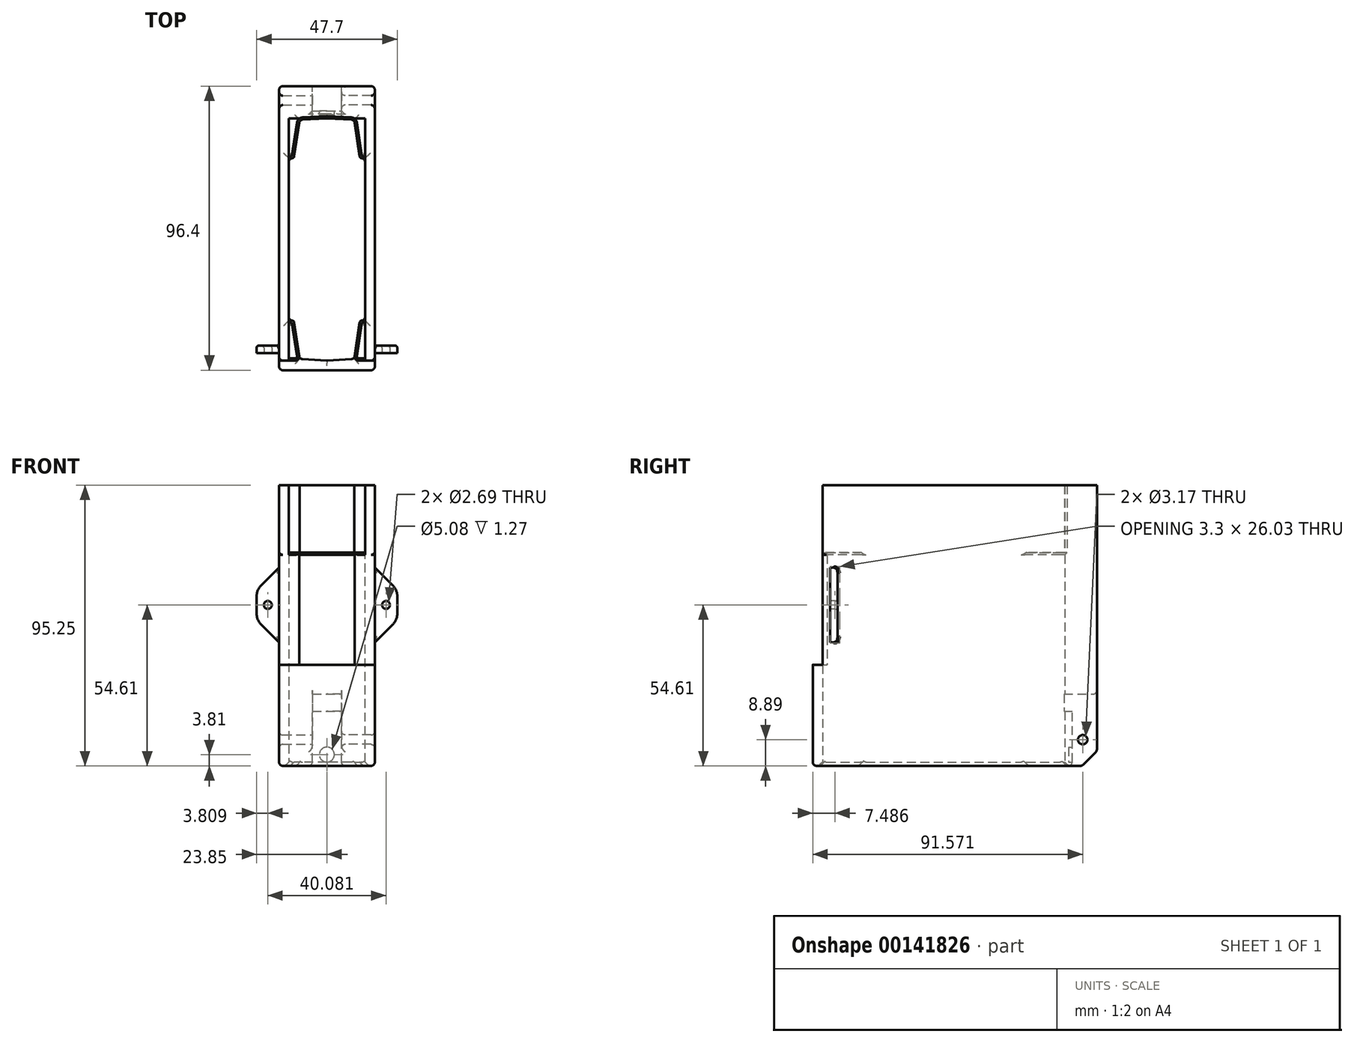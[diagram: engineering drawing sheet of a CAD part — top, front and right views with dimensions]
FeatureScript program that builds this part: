
annotation { "Feature Type Name" : "Feature", "Feature Type Description" : "" }
export const myFeature = defineFeature(function(context is Context, id is Id, definition is map)
    precondition{}
    {
        {
            var Q0;
            Q0=qCreatedBy(makeId("Top.planeOp"),FACE);
            var sketch = newSketch(context, id + "F0", { "sketchPlane" : qUnion([Q0])});
            skLineSegment(sketch, "E0.left", {"start": v(12.94, -27.53) * mm, "end": v(12.94, 27.53) * mm});
            skLineSegment(sketch, "E0.right", {"start": v(-12.94, -27.53) * mm, "end": v(-12.94, 27.53) * mm});
            skPoint(sketch, "E0.middle", {"position": v(0, 0) * mm});
            skLineSegment(sketch, "E1.top", {"start": v(12.94, -27.53) * mm, "end": v(11.21, -27.53) * mm});
            skPoint(sketch, "E2.orphan", {"position": v(12.94, -41.05) * mm});
            skLineSegment(sketch, "E3", {"start": v(11.21, -27.53) * mm, "end": v(9.28, -40.56) * mm});
            skLineSegment(sketch, "E4", {"start": v(0, -41.1) * mm, "end": v(9.28, -40.56) * mm});
            skPoint(sketch, "E0.bottom.start.orphan", {"position": v(11.21, -41.05) * mm});
            skPoint(sketch, "E5.orphan", {"position": v(9.2, -41.05) * mm});
            skLineSegment(sketch, "E6.MirrorCS", {"start": v(0, -41.1) * mm, "end": v(-9.28, -40.56) * mm});
            skLineSegment(sketch, "E7.MirrorCS", {"start": v(-11.21, -27.53) * mm, "end": v(-9.28, -40.56) * mm});
            skLineSegment(sketch, "E8.MirrorCS", {"start": v(-12.94, -27.53) * mm, "end": v(-11.21, -27.53) * mm});
            skLineSegment(sketch, "E9.MirrorCS", {"start": v(-12.94, 27.53) * mm, "end": v(-11.21, 27.53) * mm});
            skLineSegment(sketch, "E10.MirrorCS", {"start": v(-11.21, 27.53) * mm, "end": v(-9.28, 40.56) * mm});
            skLineSegment(sketch, "E11.MirrorCS", {"start": v(0, 41.1) * mm, "end": v(-9.28, 40.56) * mm});
            skLineSegment(sketch, "E12.MirrorCS", {"start": v(0, 41.1) * mm, "end": v(9.28, 40.56) * mm});
            skLineSegment(sketch, "E13.MirrorCS", {"start": v(11.21, 27.53) * mm, "end": v(9.28, 40.56) * mm});
            skLineSegment(sketch, "E14.MirrorCS", {"start": v(12.94, 27.53) * mm, "end": v(11.21, 27.53) * mm});
            skPoint(sketch, "E15.orphan", {"position": v(-12.94, -41.1) * mm});
            skPoint(sketch, "E16.orphan", {"position": v(-12.94, 41.05) * mm});
            skPoint(sketch, "E17.orphan", {"position": v(12.94, 41.1) * mm});
            skLineSegment(sketch, "E18.bottom", {"start": v(16.23, -44.39) * mm, "end": v(-16.23, -44.39) * mm});
            skLineSegment(sketch, "E18.top", {"start": v(16.23, 44.39) * mm, "end": v(-16.23, 44.39) * mm});
            skLineSegment(sketch, "E18.left", {"start": v(16.23, -44.39) * mm, "end": v(16.23, 44.39) * mm});
            skLineSegment(sketch, "E18.right", {"start": v(-16.23, -44.39) * mm, "end": v(-16.23, 44.39) * mm});
            skLineSegment(sketch, "E19", {"start": v(0, -41.1) * mm, "end": v(0, 41.1) * mm});
            skSolve(sketch);
        }
        {
            var Q0;
            Q0=makeQuery(id+"F0.imprint","IMPRINT",FACE,{"disambiguationData":[TD([[makeQuery(id+"F0.imprint","IMPRINT",EDGE,{"derivedFrom":sQuery(id+"F0.wireOp",EDGE,"E0.left")}),-1.0]])]});
            extrude(context, id + "F1", {"entities" : qUnion([Q0]), "depth" : 72.39 * mm});
        }
        {
            var Q0;
            Q0=makeQuery(id+"F1.opExtrude","SWEPT_FACE",FACE,{"disambiguationData":[OSD([sQuery(id+"F0.wireOp",EDGE,"E18.top")])]});
            var sketch = newSketch(context, id + "F2", { "sketchPlane" : qUnion([Q0])});
            skLineSegment(sketch, "E20.bottom", {"start": v(4.95, 24.36) * mm, "end": v(-4.95, 24.36) * mm});
            skLineSegment(sketch, "E20.top", {"start": v(4.95, 18.52) * mm, "end": v(-4.95, 18.52) * mm});
            skLineSegment(sketch, "E20.left", {"start": v(4.95, 24.36) * mm, "end": v(4.95, 18.52) * mm});
            skLineSegment(sketch, "E20.right", {"start": v(-4.95, 24.36) * mm, "end": v(-4.95, 18.52) * mm});
            skPoint(sketch, "E20.middle", {"position": v(0, 21.44) * mm});
            skSolve(sketch);
        }
        {
            var Q0;
            Q0=makeQuery(id+"F2.imprint","IMPRINT",FACE,{"disambiguationData":[TD([[makeQuery(id+"F2.imprint","IMPRINT",EDGE,{"derivedFrom":sQuery(id+"F2.wireOp",EDGE,"E20.bottom")}),1.0]])]});
            extrude(context, id + "F3", {"entities" : qUnion([Q0]), "operationType" : NewBodyOperationType.REMOVE, "endBound" : BoundingType.UP_TO_NEXT, "oppositeDirection" : true, "depth" : 25.4 * mm});
        }
        {
            var Q0;
            Q0=makeQuery(id+"F1.opExtrude","SWEPT_FACE",FACE,{"disambiguationData":[OSD([sQuery(id+"F0.wireOp",EDGE,"E18.top")])]});
            extrude(context, id + "F4", {"entities" : qUnion([Q0]), "operationType" : NewBodyOperationType.ADD, "depth" : 7.62 * mm});
        }
        {
            var Q0;
            {var subQ0=sQuery(id+"F0.wireOp",EDGE,"E18.top");Q0=makeQuery(id+"F4.opExtrude","CAP_EDGE",EDGE,{"disambiguationData":[OSD([subQ0]),TDD([makeQuery(id+"F1.opExtrude","CAP_EDGE",EDGE,{"disambiguationData":[OSD([subQ0])],"isStart":true})])],"isStart":false});}
            chamfer(context, id + "F5", {"entities" : qUnion([Q0]), "width" : 5.08 * mm, "tangentPropagation" : true});
        }
        {
            var Q0;
            {var subQ0=sQuery(id+"F2.wireOp",EDGE,"E20.top");Q0=makeQuery(id+"F4.boolean.opBoolean","MERGE",FACE,{"derivedFrom":[makeQuery(id+"F3.boolean.opBoolean","COPY",FACE,{"derivedFrom":makeQuery(id+"F3.opExtrude","SWEPT_FACE",FACE,{"disambiguationData":[OSD([subQ0])]})}),makeQuery(id+"F4.opExtrude","SWEPT_FACE",FACE,{"disambiguationData":[OSD([subQ0])]})]});}
            var sketch = newSketch(context, id + "F6", { "sketchPlane" : qUnion([Q0])});
            skLineSegment(sketch, "E21.bottom", {"start": v(-4.95, 52) * mm, "end": v(4.95, 52) * mm});
            skLineSegment(sketch, "E21.top", {"start": v(-4.95, 43.62) * mm, "end": v(4.95, 43.62) * mm});
            skLineSegment(sketch, "E21.left", {"start": v(-4.95, 52) * mm, "end": v(-4.95, 43.62) * mm});
            skLineSegment(sketch, "E21.right", {"start": v(4.95, 52) * mm, "end": v(4.95, 43.62) * mm});
            skSolve(sketch);
        }
        {
            var Q0;
            Q0=makeQuery(id+"F6.imprint","IMPRINT",FACE,{"disambiguationData":[TD([[makeQuery(id+"F6.imprint","IMPRINT",EDGE,{"derivedFrom":sQuery(id+"F6.wireOp",EDGE,"E21.bottom")}),-1.0]])]});
            extrude(context, id + "F7", {"entities" : qUnion([Q0]), "operationType" : NewBodyOperationType.REMOVE, "oppositeDirection" : true, "depth" : 25.4 * mm});
        }
        {
            var Q0;
            Q0=makeQuery(id+"F7.boolean.opBoolean","COPY",FACE,{"derivedFrom":makeQuery(id+"F7.opExtrude","SWEPT_FACE",FACE,{"disambiguationData":[OSD([sQuery(id+"F6.wireOp",EDGE,"E21.top")])]})});
            var sketch = newSketch(context, id + "F8", { "sketchPlane" : qUnion([Q0])});
            skCircle(sketch, "E22", {"center": v(0, 3.81) * mm, "radius": 2.54 * mm});
            skSolve(sketch);
        }
        {
            var Q0;
            Q0=makeQuery(id+"F8.imprint","IMPRINT",FACE,{"disambiguationData":[TD([[makeQuery(id+"F8.imprint","IMPRINT",EDGE,{"derivedFrom":sQuery(id+"F8.wireOp",EDGE,"E22")}),1.0]])]});
            extrude(context, id + "F9", {"entities" : qUnion([Q0]), "operationType" : NewBodyOperationType.REMOVE, "oppositeDirection" : true, "depth" : 1.27 * mm});
        }
        {
            var Q0;
            Q0=makeQuery(id+"F1.opExtrude","CAP_EDGE",EDGE,{"disambiguationData":[OSD([sQuery(id+"F0.wireOp",EDGE,"E0.right")])],"isStart":true});
            var Q1;
            Q1=makeQuery(id+"F1.opExtrude","CAP_EDGE",EDGE,{"disambiguationData":[OSD([sQuery(id+"F0.wireOp",EDGE,"E8.MirrorCS")])],"isStart":true});
            var Q2;
            Q2=makeQuery(id+"F1.opExtrude","CAP_EDGE",EDGE,{"disambiguationData":[OSD([sQuery(id+"F0.wireOp",EDGE,"E7.MirrorCS")])],"isStart":true});
            var Q3;
            Q3=makeQuery(id+"F1.opExtrude","CAP_EDGE",EDGE,{"disambiguationData":[OSD([sQuery(id+"F0.wireOp",EDGE,"E6.MirrorCS")])],"isStart":true});
            var Q4;
            Q4=makeQuery(id+"F1.opExtrude","CAP_EDGE",EDGE,{"disambiguationData":[OSD([sQuery(id+"F0.wireOp",EDGE,"E4")])],"isStart":true});
            var Q5;
            Q5=makeQuery(id+"F1.opExtrude","CAP_EDGE",EDGE,{"disambiguationData":[OSD([sQuery(id+"F0.wireOp",EDGE,"E3")])],"isStart":true});
            var Q6;
            Q6=makeQuery(id+"F1.opExtrude","CAP_EDGE",EDGE,{"disambiguationData":[OSD([sQuery(id+"F0.wireOp",EDGE,"E1.top")])],"isStart":true});
            var Q7;
            Q7=makeQuery(id+"F1.opExtrude","CAP_EDGE",EDGE,{"disambiguationData":[OSD([sQuery(id+"F0.wireOp",EDGE,"E0.left")])],"isStart":true});
            var Q8;
            Q8=makeQuery(id+"F1.opExtrude","CAP_EDGE",EDGE,{"disambiguationData":[OSD([sQuery(id+"F0.wireOp",EDGE,"E14.MirrorCS")])],"isStart":true});
            var Q9;
            Q9=makeQuery(id+"F1.opExtrude","CAP_EDGE",EDGE,{"disambiguationData":[OSD([sQuery(id+"F0.wireOp",EDGE,"E13.MirrorCS")])],"isStart":true});
            var Q10;
            Q10=makeQuery(id+"F1.opExtrude","CAP_EDGE",EDGE,{"disambiguationData":[OSD([sQuery(id+"F0.wireOp",EDGE,"E12.MirrorCS")])],"isStart":true});
            var Q11;
            Q11=makeQuery(id+"F1.opExtrude","CAP_EDGE",EDGE,{"disambiguationData":[OSD([sQuery(id+"F0.wireOp",EDGE,"E11.MirrorCS")])],"isStart":true});
            var Q12;
            Q12=makeQuery(id+"F1.opExtrude","CAP_EDGE",EDGE,{"disambiguationData":[OSD([sQuery(id+"F0.wireOp",EDGE,"E10.MirrorCS")])],"isStart":true});
            var Q13;
            Q13=makeQuery(id+"F1.opExtrude","CAP_EDGE",EDGE,{"disambiguationData":[OSD([sQuery(id+"F0.wireOp",EDGE,"E9.MirrorCS")])],"isStart":true});
            chamfer(context, id + "F10", {"entities" : qUnion([Q0, Q1, Q2, Q3, Q4, Q5, Q6, Q7, Q8, Q9, Q10, Q11, Q12, Q13]), "width" : 1.27 * mm, "tangentPropagation" : true});
        }
        {
            var Q0;
            Q0=makeQuery(id+"F1.opExtrude","SWEPT_EDGE",EDGE,{"disambiguationData":[OSD([sQuery(id+"F0.wireOp",EDGE,"E7.MirrorCS"),sQuery(id+"F0.wireOp",EDGE,"E8.MirrorCS")])]});
            var Q1;
            Q1=makeQuery(id+"F1.opExtrude","SWEPT_EDGE",EDGE,{"disambiguationData":[OSD([sQuery(id+"F0.wireOp",EDGE,"E1.top"),sQuery(id+"F0.wireOp",EDGE,"E3")])]});
            var Q2;
            Q2=makeQuery(id+"F1.opExtrude","SWEPT_EDGE",EDGE,{"disambiguationData":[OSD([sQuery(id+"F0.wireOp",EDGE,"E9.MirrorCS"),sQuery(id+"F0.wireOp",EDGE,"E10.MirrorCS")])]});
            var Q3;
            Q3=makeQuery(id+"F1.opExtrude","SWEPT_EDGE",EDGE,{"disambiguationData":[OSD([sQuery(id+"F0.wireOp",EDGE,"E13.MirrorCS"),sQuery(id+"F0.wireOp",EDGE,"E14.MirrorCS")])]});
            fillet(context, id + "F11", {"entities" : qUnion([Q0, Q1, Q2, Q3]), "radius" : 0.76 * mm, "tangentPropagation" : true, "allowEdgeOverflow" : false});
        }
        {
            var Q0;
            {var subQ0=sQuery(id+"F0.wireOp",EDGE,"E18.top");Q0=makeQuery(id+"F4.boolean.opBoolean","MERGE",FACE,{"derivedFrom":[makeQuery(id+"F1.opExtrude","CAP_FACE",FACE,{"disambiguationData":[OSD([sQuery(id+"F0.wireOp",EDGE,"E0.left"),sQuery(id+"F0.wireOp",EDGE,"E0.right"),sQuery(id+"F0.wireOp",EDGE,"E1.top"),sQuery(id+"F0.wireOp",EDGE,"E3"),sQuery(id+"F0.wireOp",EDGE,"E4"),sQuery(id+"F0.wireOp",EDGE,"E6.MirrorCS"),sQuery(id+"F0.wireOp",EDGE,"E7.MirrorCS"),sQuery(id+"F0.wireOp",EDGE,"E8.MirrorCS"),sQuery(id+"F0.wireOp",EDGE,"E9.MirrorCS"),sQuery(id+"F0.wireOp",EDGE,"E10.MirrorCS"),sQuery(id+"F0.wireOp",EDGE,"E11.MirrorCS"),sQuery(id+"F0.wireOp",EDGE,"E12.MirrorCS"),sQuery(id+"F0.wireOp",EDGE,"E13.MirrorCS"),sQuery(id+"F0.wireOp",EDGE,"E14.MirrorCS"),sQuery(id+"F0.wireOp",EDGE,"E18.bottom"),subQ0,sQuery(id+"F0.wireOp",EDGE,"E18.left"),sQuery(id+"F0.wireOp",EDGE,"E18.right")])],"isStart":true}),makeQuery(id+"F4.opExtrude","SWEPT_FACE",FACE,{"disambiguationData":[OSD([subQ0]),TDD([makeQuery(id+"F1.opExtrude","CAP_EDGE",EDGE,{"disambiguationData":[OSD([subQ0])],"isStart":true})])]})]});}
            var Q1;
            {var subQ0=sQuery(id+"F0.wireOp",EDGE,"E18.left");var subQ1=sQuery(id+"F0.wireOp",EDGE,"E18.top");Q1=makeQuery(id+"F5.opChamfer","BLEND_EDGE",EDGE,{"blendedFrom":[makeQuery(id+"F4.opExtrude","CAP_EDGE",EDGE,{"disambiguationData":[OSD([subQ1]),TDD([makeQuery(id+"F1.opExtrude","CAP_EDGE",EDGE,{"disambiguationData":[OSD([subQ1])],"isStart":true})])],"isStart":false}),makeQuery(id+"F4.boolean.opBoolean","MERGE",FACE,{"derivedFrom":[makeQuery(id+"F1.opExtrude","SWEPT_FACE",FACE,{"disambiguationData":[OSD([subQ0])]}),makeQuery(id+"F4.opExtrude","SWEPT_FACE",FACE,{"disambiguationData":[OSD([subQ1,subQ0])]})]})],"blendedInto":[makeQuery(id+"F4.boolean.opBoolean","MERGE",FACE,{"derivedFrom":[makeQuery(id+"F1.opExtrude","SWEPT_FACE",FACE,{"disambiguationData":[OSD([subQ0])]}),makeQuery(id+"F4.opExtrude","SWEPT_FACE",FACE,{"disambiguationData":[OSD([subQ1,subQ0])]})]})]});}
            var Q2;
            Q2=makeQuery(id+"F4.opExtrude","CAP_EDGE",EDGE,{"disambiguationData":[OSD([sQuery(id+"F0.wireOp",EDGE,"E18.top"),sQuery(id+"F0.wireOp",EDGE,"E18.left")])],"isStart":false});
            var Q3;
            {var subQ1=sQuery(id+"F0.wireOp",EDGE,"E18.left");var subQ2=sQuery(id+"F0.wireOp",EDGE,"E18.top");var subQ3=makeQuery(id+"F4.opExtrude","CAP_FACE",FACE,{"disambiguationData":[OSD([subQ2])],"isStart":false});Q3=makeQuery(id+"F7.boolean.opBoolean","SPLIT",EDGE,{"disambiguationData":[TD([makeQuery(id+"F1.opExtrude","SWEPT_FACE",FACE,{"disambiguationData":[OSD([subQ1])]})])],"derivedFrom":makeQuery(id+"F5.opChamfer","BLEND_EDGE",EDGE,{"blendedFrom":[makeQuery(id+"F4.opExtrude","CAP_EDGE",EDGE,{"disambiguationData":[OSD([subQ2]),TDD([makeQuery(id+"F1.opExtrude","CAP_EDGE",EDGE,{"disambiguationData":[OSD([subQ2])],"isStart":true})])],"isStart":false}),subQ3],"blendedInto":[subQ3]})});}
            var Q4;
            Q4=makeQuery(id+"F7.boolean.opBoolean","MERGE",EDGE,{"derivedFrom":[makeQuery(id+"F4.opExtrude","CAP_EDGE",EDGE,{"disambiguationData":[OSD([sQuery(id+"F2.wireOp",EDGE,"E20.right")])],"isStart":false}),makeQuery(id+"F7.opExtrude","SWEPT_EDGE",EDGE,{"disambiguationData":[OSD([sQuery(id+"F6.wireOp",EDGE,"E21.bottom"),sQuery(id+"F6.wireOp",EDGE,"E21.right")])]})]});
            var Q5;
            {var subQ1=sQuery(id+"F0.wireOp",EDGE,"E18.top");var subQ2=makeQuery(id+"F4.opExtrude","CAP_FACE",FACE,{"disambiguationData":[OSD([subQ1])],"isStart":false});var subQ3=sQuery(id+"F0.wireOp",EDGE,"E18.right");Q5=makeQuery(id+"F7.boolean.opBoolean","SPLIT",EDGE,{"disambiguationData":[TD([makeQuery(id+"F1.opExtrude","SWEPT_FACE",FACE,{"disambiguationData":[OSD([subQ3])]})])],"derivedFrom":makeQuery(id+"F5.opChamfer","BLEND_EDGE",EDGE,{"blendedFrom":[makeQuery(id+"F4.opExtrude","CAP_EDGE",EDGE,{"disambiguationData":[OSD([subQ1]),TDD([makeQuery(id+"F1.opExtrude","CAP_EDGE",EDGE,{"disambiguationData":[OSD([subQ1])],"isStart":true})])],"isStart":false}),subQ2],"blendedInto":[subQ2]})});}
            var Q6;
            Q6=makeQuery(id+"F7.boolean.opBoolean","INTERSECT",EDGE,{"derivedFrom":[makeQuery(id+"F5.opChamfer","BLEND_FACE",FACE,{"disambiguationData":[OSD([sQuery(id+"F0.wireOp",EDGE,"E18.top")])]}),makeQuery(id+"F7.opExtrude","SWEPT_FACE",FACE,{"disambiguationData":[OSD([sQuery(id+"F6.wireOp",EDGE,"E21.right")])]})]});
            var Q7;
            Q7=makeQuery(id+"F7.boolean.opBoolean","INTERSECT",EDGE,{"derivedFrom":[makeQuery(id+"F5.opChamfer","BLEND_FACE",FACE,{"disambiguationData":[OSD([sQuery(id+"F0.wireOp",EDGE,"E18.top")])]}),makeQuery(id+"F7.opExtrude","SWEPT_FACE",FACE,{"disambiguationData":[OSD([sQuery(id+"F6.wireOp",EDGE,"E21.left")])]})]});
            var Q8;
            Q8=makeQuery(id+"F4.opExtrude","CAP_EDGE",EDGE,{"disambiguationData":[OSD([sQuery(id+"F0.wireOp",EDGE,"E18.top"),sQuery(id+"F0.wireOp",EDGE,"E18.right")])],"isStart":false});
            var Q9;
            {var subQ0=sQuery(id+"F0.wireOp",EDGE,"E18.right");var subQ1=sQuery(id+"F0.wireOp",EDGE,"E18.top");Q9=makeQuery(id+"F5.opChamfer","BLEND_EDGE",EDGE,{"blendedFrom":[makeQuery(id+"F4.opExtrude","CAP_EDGE",EDGE,{"disambiguationData":[OSD([subQ1]),TDD([makeQuery(id+"F1.opExtrude","CAP_EDGE",EDGE,{"disambiguationData":[OSD([subQ1])],"isStart":true})])],"isStart":false}),makeQuery(id+"F4.boolean.opBoolean","MERGE",FACE,{"derivedFrom":[makeQuery(id+"F1.opExtrude","SWEPT_FACE",FACE,{"disambiguationData":[OSD([subQ0])]}),makeQuery(id+"F4.opExtrude","SWEPT_FACE",FACE,{"disambiguationData":[OSD([subQ1,subQ0])]})]})],"blendedInto":[makeQuery(id+"F4.boolean.opBoolean","MERGE",FACE,{"derivedFrom":[makeQuery(id+"F1.opExtrude","SWEPT_FACE",FACE,{"disambiguationData":[OSD([subQ0])]}),makeQuery(id+"F4.opExtrude","SWEPT_FACE",FACE,{"disambiguationData":[OSD([subQ1,subQ0])]})]})]});}
            var Q10;
            Q10=makeQuery(id+"F4.opExtrude","CAP_EDGE",EDGE,{"disambiguationData":[OSD([sQuery(id+"F2.wireOp",EDGE,"E20.bottom")])],"isStart":false});
            var Q11;
            Q11=makeQuery(id+"F7.boolean.opBoolean","MERGE",EDGE,{"derivedFrom":[makeQuery(id+"F4.opExtrude","CAP_EDGE",EDGE,{"disambiguationData":[OSD([sQuery(id+"F2.wireOp",EDGE,"E20.left")])],"isStart":false}),makeQuery(id+"F7.opExtrude","SWEPT_EDGE",EDGE,{"disambiguationData":[OSD([sQuery(id+"F6.wireOp",EDGE,"E21.bottom"),sQuery(id+"F6.wireOp",EDGE,"E21.left")])]})]});
            var Q12;
            Q12=makeQuery(id+"F1.opExtrude","SWEPT_EDGE",EDGE,{"disambiguationData":[OSD([sQuery(id+"F0.wireOp",EDGE,"E18.bottom"),sQuery(id+"F0.wireOp",EDGE,"E18.right")])]});
            var Q13;
            Q13=makeQuery(id+"F1.opExtrude","SWEPT_EDGE",EDGE,{"disambiguationData":[OSD([sQuery(id+"F0.wireOp",EDGE,"E18.bottom"),sQuery(id+"F0.wireOp",EDGE,"E18.left")])]});
            var Q14;
            Q14=makeQuery(id+"F1.opExtrude","SWEPT_EDGE",EDGE,{"disambiguationData":[OSD([sQuery(id+"F0.wireOp",EDGE,"E0.left"),sQuery(id+"F0.wireOp",EDGE,"E14.MirrorCS")])]});
            var Q15;
            Q15=makeQuery(id+"F1.opExtrude","SWEPT_EDGE",EDGE,{"disambiguationData":[OSD([sQuery(id+"F0.wireOp",EDGE,"E12.MirrorCS"),sQuery(id+"F0.wireOp",EDGE,"E13.MirrorCS")])]});
            var Q16;
            {var subQ0=sQuery(id+"F0.wireOp",EDGE,"E12.MirrorCS");var subQ1=sQuery(id+"F0.wireOp",EDGE,"E11.MirrorCS");Q16=makeQuery(id+"F3.boolean.opBoolean","SPLIT",EDGE,{"disambiguationData":[TD([makeQuery(id+"F3.opExtrude","SWEPT_FACE",FACE,{"disambiguationData":[OSD([sQuery(id+"F2.wireOp",EDGE,"E20.bottom")])]})])],"derivedFrom":makeQuery(id+"F1.opExtrude","SWEPT_EDGE",EDGE,{"disambiguationData":[OSD([subQ1,subQ0])]})});}
            var Q17;
            {var subQ0=sQuery(id+"F0.wireOp",EDGE,"E12.MirrorCS");var subQ1=sQuery(id+"F0.wireOp",EDGE,"E11.MirrorCS");Q17=makeQuery(id+"F3.boolean.opBoolean","SPLIT",EDGE,{"disambiguationData":[TD([makeQuery(id+"F3.opExtrude","SWEPT_FACE",FACE,{"disambiguationData":[OSD([sQuery(id+"F2.wireOp",EDGE,"E20.top")])]})])],"derivedFrom":makeQuery(id+"F1.opExtrude","SWEPT_EDGE",EDGE,{"disambiguationData":[OSD([subQ1,subQ0])]})});}
            var Q18;
            Q18=makeQuery(id+"F1.opExtrude","SWEPT_EDGE",EDGE,{"disambiguationData":[OSD([sQuery(id+"F0.wireOp",EDGE,"E10.MirrorCS"),sQuery(id+"F0.wireOp",EDGE,"E11.MirrorCS")])]});
            var Q19;
            Q19=makeQuery(id+"F1.opExtrude","SWEPT_EDGE",EDGE,{"disambiguationData":[OSD([sQuery(id+"F0.wireOp",EDGE,"E0.right"),sQuery(id+"F0.wireOp",EDGE,"E9.MirrorCS")])]});
            var Q20;
            Q20=makeQuery(id+"F1.opExtrude","SWEPT_EDGE",EDGE,{"disambiguationData":[OSD([sQuery(id+"F0.wireOp",EDGE,"E0.right"),sQuery(id+"F0.wireOp",EDGE,"E8.MirrorCS")])]});
            var Q21;
            Q21=makeQuery(id+"F1.opExtrude","SWEPT_EDGE",EDGE,{"disambiguationData":[OSD([sQuery(id+"F0.wireOp",EDGE,"E6.MirrorCS"),sQuery(id+"F0.wireOp",EDGE,"E7.MirrorCS")])]});
            var Q22;
            Q22=makeQuery(id+"F1.opExtrude","SWEPT_EDGE",EDGE,{"disambiguationData":[OSD([sQuery(id+"F0.wireOp",EDGE,"E4"),sQuery(id+"F0.wireOp",EDGE,"E6.MirrorCS")])]});
            var Q23;
            Q23=makeQuery(id+"F1.opExtrude","SWEPT_EDGE",EDGE,{"disambiguationData":[OSD([sQuery(id+"F0.wireOp",EDGE,"E3"),sQuery(id+"F0.wireOp",EDGE,"E4")])]});
            var Q24;
            Q24=makeQuery(id+"F1.opExtrude","SWEPT_EDGE",EDGE,{"disambiguationData":[OSD([sQuery(id+"F0.wireOp",EDGE,"E0.left"),sQuery(id+"F0.wireOp",EDGE,"E1.top")])]});
            fillet(context, id + "F12", {"entities" : qUnion([Q0, Q1, Q2, Q3, Q4, Q5, Q6, Q7, Q8, Q9, Q10, Q11, Q12, Q13, Q14, Q15, Q16, Q17, Q18, Q19, Q20, Q21, Q22, Q23, Q24]), "radius" : 1.27 * mm, "tangentPropagation" : true, "allowEdgeOverflow" : false});
        }
        {
            var Q0;
            {var subQ0=sQuery(id+"F2.wireOp",EDGE,"E20.left");Q0=makeQuery(id+"F7.boolean.opBoolean","MERGE",FACE,{"derivedFrom":[makeQuery(id+"F4.boolean.opBoolean","MERGE",FACE,{"derivedFrom":[makeQuery(id+"F3.boolean.opBoolean","COPY",FACE,{"derivedFrom":makeQuery(id+"F3.opExtrude","SWEPT_FACE",FACE,{"disambiguationData":[OSD([subQ0])]})}),makeQuery(id+"F4.opExtrude","SWEPT_FACE",FACE,{"disambiguationData":[OSD([subQ0])]})]}),makeQuery(id+"F7.opExtrude","SWEPT_FACE",FACE,{"disambiguationData":[OSD([sQuery(id+"F6.wireOp",EDGE,"E21.left")])]})]});}
            var sketch = newSketch(context, id + "F13", { "sketchPlane" : qUnion([Q0])});
            skLineSegment(sketch, "E23", {"start": v(43.62, 8.89) * mm, "end": v(50.74, 8.89) * mm});
            skCircle(sketch, "E24", {"center": v(47.18, 8.89) * mm, "radius": 1.59 * mm});
            skLineSegment(sketch, "E25", {"start": v(43.62, 1.27) * mm, "end": v(46.4, 1.27) * mm});
            skSolve(sketch);
        }
        {
            var Q0;
            {var subQ0=sQuery(id+"F13.wireOp",EDGE,"E24");var subQ1=sQuery(id+"F13.wireOp",EDGE,"E23");var subQ2=makeQuery(id+"F13.imprint","INTERSECT",VERTEX,{"disambiguationData":[OD(0.0)],"derivedFrom":[subQ1,subQ0]});Q0=makeQuery(id+"F13.imprint","IMPRINT",FACE,{"disambiguationData":[TD([[makeQuery(id+"F13.imprint","IMPRINT",EDGE,{"disambiguationData":[TD([[subQ2,-1.0]])],"derivedFrom":subQ1}),1.0]])]});}
            var Q1;
            {var subQ0=sQuery(id+"F13.wireOp",EDGE,"E24");var subQ1=sQuery(id+"F13.wireOp",EDGE,"E23");var subQ2=makeQuery(id+"F13.imprint","INTERSECT",VERTEX,{"disambiguationData":[OD(0.0)],"derivedFrom":[subQ1,subQ0]});Q1=makeQuery(id+"F13.imprint","IMPRINT",FACE,{"disambiguationData":[TD([[makeQuery(id+"F13.imprint","IMPRINT",EDGE,{"disambiguationData":[TD([[subQ2,-1.0]])],"derivedFrom":subQ1}),-1.0]])]});}
            extrude(context, id + "F14", {"entities" : qUnion([Q0, Q1]), "operationType" : NewBodyOperationType.REMOVE, "endBound" : BoundingType.THROUGH_ALL, "depth" : 25.4 * mm});
        }
        {
            var Q0;
            {var subQ0=sQuery(id+"F13.wireOp",EDGE,"E24");var subQ1=sQuery(id+"F13.wireOp",EDGE,"E23");var subQ2=makeQuery(id+"F13.imprint","INTERSECT",VERTEX,{"disambiguationData":[OD(0.0)],"derivedFrom":[subQ1,subQ0]});Q0=makeQuery(id+"F13.imprint","IMPRINT",FACE,{"disambiguationData":[TD([[makeQuery(id+"F13.imprint","IMPRINT",EDGE,{"disambiguationData":[TD([[subQ2,-1.0]])],"derivedFrom":subQ1}),-1.0]])]});}
            var Q1;
            {var subQ0=sQuery(id+"F13.wireOp",EDGE,"E24");var subQ1=sQuery(id+"F13.wireOp",EDGE,"E23");var subQ2=makeQuery(id+"F13.imprint","INTERSECT",VERTEX,{"disambiguationData":[OD(0.0)],"derivedFrom":[subQ1,subQ0]});Q1=makeQuery(id+"F13.imprint","IMPRINT",FACE,{"disambiguationData":[TD([[makeQuery(id+"F13.imprint","IMPRINT",EDGE,{"disambiguationData":[TD([[subQ2,-1.0]])],"derivedFrom":subQ1}),1.0]])]});}
            extrude(context, id + "F15", {"entities" : qUnion([Q0, Q1]), "operationType" : NewBodyOperationType.REMOVE, "endBound" : BoundingType.THROUGH_ALL, "oppositeDirection" : true, "depth" : 25.4 * mm});
        }
        {
            var Q0;
            {var subQ0=sQuery(id+"F0.wireOp",EDGE,"E18.left");Q0=makeQuery(id+"F14.boolean.opBoolean","INTERSECT",EDGE,{"derivedFrom":[makeQuery(id+"F4.boolean.opBoolean","MERGE",FACE,{"derivedFrom":[makeQuery(id+"F1.opExtrude","SWEPT_FACE",FACE,{"disambiguationData":[OSD([subQ0])]}),makeQuery(id+"F4.opExtrude","SWEPT_FACE",FACE,{"disambiguationData":[OSD([sQuery(id+"F0.wireOp",EDGE,"E18.top"),subQ0])]})]}),makeQuery(id+"F14.opExtrude","SWEPT_FACE",FACE,{"disambiguationData":[OSD([sQuery(id+"F13.wireOp",EDGE,"E24")])]})]});}
            var Q1;
            Q1=makeQuery(id+"F15.boolean.opBoolean","COPY",EDGE,{"derivedFrom":makeQuery(id+"F15.opExtrude","CAP_EDGE",EDGE,{"disambiguationData":[OSD([sQuery(id+"F13.wireOp",EDGE,"E24")])],"isStart":true})});
            var Q2;
            {var subQ0=sQuery(id+"F2.wireOp",EDGE,"E20.right");Q2=makeQuery(id+"F14.boolean.opBoolean","INTERSECT",EDGE,{"derivedFrom":[makeQuery(id+"F7.boolean.opBoolean","MERGE",FACE,{"derivedFrom":[makeQuery(id+"F4.boolean.opBoolean","MERGE",FACE,{"derivedFrom":[makeQuery(id+"F3.boolean.opBoolean","COPY",FACE,{"derivedFrom":makeQuery(id+"F3.opExtrude","SWEPT_FACE",FACE,{"disambiguationData":[OSD([subQ0])]})}),makeQuery(id+"F4.opExtrude","SWEPT_FACE",FACE,{"disambiguationData":[OSD([subQ0])]})]}),makeQuery(id+"F7.opExtrude","SWEPT_FACE",FACE,{"disambiguationData":[OSD([sQuery(id+"F6.wireOp",EDGE,"E21.right")])]})]}),makeQuery(id+"F14.opExtrude","SWEPT_FACE",FACE,{"disambiguationData":[OSD([sQuery(id+"F13.wireOp",EDGE,"E24")])]})]});}
            var Q3;
            {var subQ0=sQuery(id+"F0.wireOp",EDGE,"E18.right");Q3=makeQuery(id+"F15.boolean.opBoolean","INTERSECT",EDGE,{"derivedFrom":[makeQuery(id+"F4.boolean.opBoolean","MERGE",FACE,{"derivedFrom":[makeQuery(id+"F1.opExtrude","SWEPT_FACE",FACE,{"disambiguationData":[OSD([subQ0])]}),makeQuery(id+"F4.opExtrude","SWEPT_FACE",FACE,{"disambiguationData":[OSD([sQuery(id+"F0.wireOp",EDGE,"E18.top"),subQ0])]})]}),makeQuery(id+"F15.opExtrude","SWEPT_FACE",FACE,{"disambiguationData":[OSD([sQuery(id+"F13.wireOp",EDGE,"E24")])]})]});}
            fillet(context, id + "F16", {"entities" : qUnion([Q0, Q1, Q2, Q3]), "radius" : 1.27 * mm, "tangentPropagation" : true, "allowEdgeOverflow" : false});
        }
        {
            var Q0;
            {var subQ0=sQuery(id+"F0.wireOp",EDGE,"E18.top");Q0=makeQuery(id+"F4.boolean.opBoolean","MERGE",FACE,{"derivedFrom":[makeQuery(id+"F1.opExtrude","CAP_FACE",FACE,{"disambiguationData":[OSD([sQuery(id+"F0.wireOp",EDGE,"E0.left"),sQuery(id+"F0.wireOp",EDGE,"E0.right"),sQuery(id+"F0.wireOp",EDGE,"E1.top"),sQuery(id+"F0.wireOp",EDGE,"E3"),sQuery(id+"F0.wireOp",EDGE,"E4"),sQuery(id+"F0.wireOp",EDGE,"E6.MirrorCS"),sQuery(id+"F0.wireOp",EDGE,"E7.MirrorCS"),sQuery(id+"F0.wireOp",EDGE,"E8.MirrorCS"),sQuery(id+"F0.wireOp",EDGE,"E9.MirrorCS"),sQuery(id+"F0.wireOp",EDGE,"E10.MirrorCS"),sQuery(id+"F0.wireOp",EDGE,"E11.MirrorCS"),sQuery(id+"F0.wireOp",EDGE,"E12.MirrorCS"),sQuery(id+"F0.wireOp",EDGE,"E13.MirrorCS"),sQuery(id+"F0.wireOp",EDGE,"E14.MirrorCS"),sQuery(id+"F0.wireOp",EDGE,"E18.bottom"),subQ0,sQuery(id+"F0.wireOp",EDGE,"E18.left"),sQuery(id+"F0.wireOp",EDGE,"E18.right")])],"isStart":false}),makeQuery(id+"F4.opExtrude","SWEPT_FACE",FACE,{"disambiguationData":[OSD([subQ0]),TDD([makeQuery(id+"F1.opExtrude","CAP_EDGE",EDGE,{"disambiguationData":[OSD([subQ0])],"isStart":false})])]})]});}
            var sketch = newSketch(context, id + "F17", { "sketchPlane" : qUnion([Q0])});
            skLineSegment(sketch, "E26.0", {"start": v(14.96, -44.39) * mm, "end": v(-14.96, -44.39) * mm});
            skLineSegment(sketch, "E27.bottom", {"start": v(-18.94, -44.39) * mm, "end": v(19.3, -44.39) * mm});
            skLineSegment(sketch, "E27.top", {"start": v(-18.94, -42.86) * mm, "end": v(19.3, -42.86) * mm});
            skLineSegment(sketch, "E27.left", {"start": v(-18.94, -44.39) * mm, "end": v(-18.94, -42.86) * mm});
            skLineSegment(sketch, "E27.right", {"start": v(19.3, -44.39) * mm, "end": v(19.3, -42.86) * mm});
            skPoint(sketch, "E28.0", {"position": v(0, -41.1) * mm});
            skLineSegment(sketch, "E29.bottom", {"start": v(19.3, -42.86) * mm, "end": v(-18.94, -42.86) * mm});
            skLineSegment(sketch, "E29.top", {"start": v(19.3, -41.1) * mm, "end": v(-18.94, -41.1) * mm});
            skLineSegment(sketch, "E29.left", {"start": v(19.3, -42.86) * mm, "end": v(19.3, -41.1) * mm});
            skLineSegment(sketch, "E29.right", {"start": v(-18.94, -42.86) * mm, "end": v(-18.94, -41.1) * mm});
            skPoint(sketch, "E30.0", {"position": v(9.43, -39.54) * mm});
            skPoint(sketch, "E31.0", {"position": v(-9.43, -39.54) * mm});
            skLineSegment(sketch, "E32.bottom", {"start": v(9.43, -39.54) * mm, "end": v(-9.43, -39.54) * mm});
            skLineSegment(sketch, "E32.top", {"start": v(9.43, -41.1) * mm, "end": v(-9.43, -41.1) * mm});
            skLineSegment(sketch, "E32.left", {"start": v(9.43, -39.54) * mm, "end": v(9.43, -41.1) * mm});
            skLineSegment(sketch, "E32.right", {"start": v(-9.43, -39.54) * mm, "end": v(-9.43, -41.1) * mm});
            skSolve(sketch);
        }
        {
            var Q0;
            {var subQ0=sQuery(id+"F0.wireOp",EDGE,"E18.top");var subQ1=sQuery(id+"F0.wireOp",EDGE,"E18.right");var subQ7=sQuery(id+"F17.wireOp",EDGE,"E27.top");var subQ8=makeQuery(id+"F4.boolean.opBoolean","MERGE",EDGE,{"derivedFrom":[makeQuery(id+"F1.opExtrude","CAP_EDGE",EDGE,{"disambiguationData":[OSD([subQ1])],"isStart":false}),makeQuery(id+"F4.opExtrude","SWEPT_EDGE",EDGE,{"disambiguationData":[OSD([subQ0,subQ1]),TDD([makeQuery(id+"F1.opExtrude","CAP_VERTEX",VERTEX,{"disambiguationData":[OSD([subQ0,subQ1])],"isStart":false})])]})]});var subQ9=makeQuery(id+"F17.imprint","INTERSECT",VERTEX,{"derivedFrom":[subQ8,subQ7]});Q0=makeQuery(id+"F17.imprint","IMPRINT",FACE,{"disambiguationData":[TD([[makeQuery(id+"F17.imprint","IMPRINT",EDGE,{"disambiguationData":[TD([[subQ9,-1.0]])],"derivedFrom":subQ7}),-1.0]])]});}
            var Q1;
            {var subQ0=sQuery(id+"F0.wireOp",EDGE,"E18.top");var subQ2=sQuery(id+"F0.wireOp",EDGE,"E18.left");var subQ7=sQuery(id+"F17.wireOp",EDGE,"E29.bottom");var subQ8=makeQuery(id+"F4.boolean.opBoolean","MERGE",EDGE,{"derivedFrom":[makeQuery(id+"F1.opExtrude","CAP_EDGE",EDGE,{"disambiguationData":[OSD([subQ2])],"isStart":false}),makeQuery(id+"F4.opExtrude","SWEPT_EDGE",EDGE,{"disambiguationData":[OSD([subQ0,subQ2]),TDD([makeQuery(id+"F1.opExtrude","CAP_VERTEX",VERTEX,{"disambiguationData":[OSD([subQ0,subQ2])],"isStart":false})])]})]});var subQ9=makeQuery(id+"F17.imprint","INTERSECT",VERTEX,{"derivedFrom":[subQ8,subQ7]});Q1=makeQuery(id+"F17.imprint","IMPRINT",FACE,{"disambiguationData":[TD([[makeQuery(id+"F17.imprint","IMPRINT",EDGE,{"disambiguationData":[TD([[subQ9,-1.0]])],"derivedFrom":subQ7}),1.0]])]});}
            var Q2;
            {var subQ0=sQuery(id+"F17.wireOp",EDGE,"E32.top");var subQ1=sQuery(id+"F17.wireOp",EDGE,"E29.top");var subQ2=makeQuery(id+"F17.imprint","INTERSECT",VERTEX,{"derivedFrom":[subQ1,subQ0,sQuery(id+"F17.wireOp",EDGE,"E32.left")]});Q2=makeQuery(id+"F17.imprint","IMPRINT",FACE,{"disambiguationData":[TD([[makeQuery(id+"F17.imprint","IMPRINT",EDGE,{"disambiguationData":[TD([[subQ2,1.0]])],"derivedFrom":subQ1}),1.0]])]});}
            var Q3;
            Q3=makeQuery(id+"F17.imprint","IMPRINT",FACE,{"disambiguationData":[TD([[makeQuery(id+"F17.imprint","IMPRINT",EDGE,{"derivedFrom":sQuery(id+"F17.wireOp",EDGE,"E32.bottom")}),1.0]])]});
            var Q4;
            {var subQ2=sQuery(id+"F17.wireOp",EDGE,"E32.right");Q4=makeQuery(id+"F17.imprint","IMPRINT",FACE,{"disambiguationData":[TD([[makeQuery(id+"F17.imprint","IMPRINT",EDGE,{"derivedFrom":subQ2}),1.0]])]});}
            var Q5;
            {var subQ2=sQuery(id+"F17.wireOp",EDGE,"E32.left");Q5=makeQuery(id+"F17.imprint","IMPRINT",FACE,{"disambiguationData":[TD([[makeQuery(id+"F17.imprint","IMPRINT",EDGE,{"derivedFrom":subQ2}),-1.0]])]});}
            extrude(context, id + "F18", {"entities" : qUnion([Q0, Q1, Q2, Q3, Q4, Q5]), "operationType" : NewBodyOperationType.REMOVE, "oppositeDirection" : true, "depth" : 38.1 * mm});
        }
        {
            var Q0;
            {var subQ0=sQuery(id+"F0.wireOp",EDGE,"E18.top");Q0=makeQuery(id+"F4.boolean.opBoolean","MERGE",FACE,{"derivedFrom":[makeQuery(id+"F1.opExtrude","CAP_FACE",FACE,{"disambiguationData":[OSD([sQuery(id+"F0.wireOp",EDGE,"E0.left"),sQuery(id+"F0.wireOp",EDGE,"E0.right"),sQuery(id+"F0.wireOp",EDGE,"E1.top"),sQuery(id+"F0.wireOp",EDGE,"E3"),sQuery(id+"F0.wireOp",EDGE,"E4"),sQuery(id+"F0.wireOp",EDGE,"E6.MirrorCS"),sQuery(id+"F0.wireOp",EDGE,"E7.MirrorCS"),sQuery(id+"F0.wireOp",EDGE,"E8.MirrorCS"),sQuery(id+"F0.wireOp",EDGE,"E9.MirrorCS"),sQuery(id+"F0.wireOp",EDGE,"E10.MirrorCS"),sQuery(id+"F0.wireOp",EDGE,"E11.MirrorCS"),sQuery(id+"F0.wireOp",EDGE,"E12.MirrorCS"),sQuery(id+"F0.wireOp",EDGE,"E13.MirrorCS"),sQuery(id+"F0.wireOp",EDGE,"E14.MirrorCS"),sQuery(id+"F0.wireOp",EDGE,"E18.bottom"),subQ0,sQuery(id+"F0.wireOp",EDGE,"E18.left"),sQuery(id+"F0.wireOp",EDGE,"E18.right")])],"isStart":false}),makeQuery(id+"F4.opExtrude","SWEPT_FACE",FACE,{"disambiguationData":[OSD([subQ0]),TDD([makeQuery(id+"F1.opExtrude","CAP_EDGE",EDGE,{"disambiguationData":[OSD([subQ0])],"isStart":false})])]})]});}
            chamfer(context, id + "F19", {"entities" : qUnion([Q0]), "width" : 0.76 * mm, "tangentPropagation" : true});
        }
        {
            var Q0;
            Q0=makeQuery(id+"F18.boolean.opBoolean","COPY",EDGE,{"derivedFrom":makeQuery(id+"F18.opExtrude","SWEPT_EDGE",EDGE,{"disambiguationData":[OSD([sQuery(id+"F17.wireOp",EDGE,"E29.top"),sQuery(id+"F17.wireOp",EDGE,"E32.top"),sQuery(id+"F17.wireOp",EDGE,"E32.left")])]})});
            var Q1;
            Q1=makeQuery(id+"F18.boolean.opBoolean","COPY",EDGE,{"derivedFrom":makeQuery(id+"F18.opExtrude","SWEPT_EDGE",EDGE,{"disambiguationData":[OSD([sQuery(id+"F17.wireOp",EDGE,"E29.top"),sQuery(id+"F17.wireOp",EDGE,"E32.top"),sQuery(id+"F17.wireOp",EDGE,"E32.right")])]})});
            var Q2;
            Q2=makeQuery(id+"F18.boolean.opBoolean","COPY",EDGE,{"derivedFrom":makeQuery(id+"F18.opExtrude","SWEPT_EDGE",EDGE,{"disambiguationData":[OSD([sQuery(id+"F0.wireOp",EDGE,"E18.top"),sQuery(id+"F0.wireOp",EDGE,"E18.left"),sQuery(id+"F17.wireOp",EDGE,"E29.top")])]})});
            var Q3;
            Q3=makeQuery(id+"F18.boolean.opBoolean","COPY",EDGE,{"derivedFrom":makeQuery(id+"F18.opExtrude","SWEPT_EDGE",EDGE,{"disambiguationData":[OSD([sQuery(id+"F0.wireOp",EDGE,"E18.top"),sQuery(id+"F0.wireOp",EDGE,"E18.right"),sQuery(id+"F17.wireOp",EDGE,"E29.top")])]})});
            fillet(context, id + "F20", {"entities" : qUnion([Q0, Q1, Q2, Q3]), "radius" : 1.27 * mm, "tangentPropagation" : true, "allowEdgeOverflow" : false});
        }
        {
            var Q0;
            {var subQ0=sQuery(id+"F17.wireOp",EDGE,"E29.top");Q0=makeQuery(id+"F18.boolean.opBoolean","COPY",FACE,{"derivedFrom":makeQuery(id+"F18.opExtrude","SWEPT_FACE",FACE,{"disambiguationData":[OSD([subQ0]),TDD([makeQuery(id+"F17.imprint","IMPRINT",EDGE,{"disambiguationData":[TD([[makeQuery(id+"F17.imprint","INTERSECT",VERTEX,{"derivedFrom":[subQ0,sQuery(id+"F17.wireOp",EDGE,"E32.top"),sQuery(id+"F17.wireOp",EDGE,"E32.right")]}),-1.0]])],"derivedFrom":subQ0})])]})});}
            var sketch = newSketch(context, id + "F21", { "sketchPlane" : qUnion([Q0])});
            skLineSegment(sketch, "E33.bottom", {"start": v(-16.23, 59.7) * mm, "end": v(-23.85, 59.7) * mm});
            skLineSegment(sketch, "E33.top", {"start": v(-16.23, 49.53) * mm, "end": v(-23.85, 49.53) * mm});
            skLineSegment(sketch, "E33.left", {"start": v(-16.23, 59.7) * mm, "end": v(-16.23, 49.53) * mm});
            skLineSegment(sketch, "E33.right", {"start": v(-23.85, 59.7) * mm, "end": v(-23.85, 49.53) * mm});
            skLineSegment(sketch, "E34", {"start": v(-23.85, 59.69) * mm, "end": v(-16.23, 67.31) * mm});
            skLineSegment(sketch, "E35", {"start": v(-23.85, 49.53) * mm, "end": v(-16.23, 41.91) * mm});
            skLineSegment(sketch, "E36.MirrorCS", {"start": v(23.85, 59.69) * mm, "end": v(16.23, 67.31) * mm});
            skLineSegment(sketch, "E37.MirrorCS", {"start": v(23.85, 59.7) * mm, "end": v(23.85, 49.53) * mm});
            skLineSegment(sketch, "E38.MirrorCS", {"start": v(23.85, 49.53) * mm, "end": v(16.23, 41.91) * mm});
            skLineSegment(sketch, "E39", {"start": v(16.23, 67.31) * mm, "end": v(16.23, 41.91) * mm});
            skCircle(sketch, "E40", {"center": v(-20.04, 54.61) * mm, "radius": 1.35 * mm});
            skPoint(sketch, "E40.centerSnap0", {"position": v(-20.04, 59.7) * mm});
            skPoint(sketch, "E40.centerSnap1", {"position": v(-23.85, 54.61) * mm});
            skCircle(sketch, "E41.MirrorC", {"center": v(20.04, 54.61) * mm, "radius": 1.35 * mm});
            skLineSegment(sketch, "E42", {"start": v(-16.23, 41.91) * mm, "end": v(-16.23, 67.31) * mm});
            skSolve(sketch);
        }
        {
            var Q0;
            Q0=makeQuery(id+"F21.imprint","IMPRINT",FACE,{"disambiguationData":[TD([[makeQuery(id+"F21.imprint","IMPRINT",EDGE,{"derivedFrom":sQuery(id+"F21.wireOp",EDGE,"E36.MirrorCS")}),1.0]])]});
            var Q1;
            {var subQ0=sQuery(id+"F21.wireOp",EDGE,"E33.top");Q1=makeQuery(id+"F21.imprint","IMPRINT",FACE,{"disambiguationData":[TD([[makeQuery(id+"F21.imprint","IMPRINT",EDGE,{"derivedFrom":subQ0}),1.0]])]});}
            var Q2;
            Q2=makeQuery(id+"F21.imprint","IMPRINT",FACE,{"disambiguationData":[TD([[makeQuery(id+"F21.imprint","IMPRINT",EDGE,{"derivedFrom":sQuery(id+"F21.wireOp",EDGE,"E33.bottom")}),1.0]])]});
            var Q3;
            {var subQ0=sQuery(id+"F21.wireOp",EDGE,"E33.bottom");Q3=makeQuery(id+"F21.imprint","IMPRINT",FACE,{"disambiguationData":[TD([[makeQuery(id+"F21.imprint","IMPRINT",EDGE,{"derivedFrom":subQ0}),-1.0]])]});}
            extrude(context, id + "F22", {"entities" : qUnion([Q0, Q1, Q2, Q3]), "operationType" : NewBodyOperationType.ADD, "oppositeDirection" : true, "depth" : 5.08 * mm});
        }
        {
            var Q0;
            Q0=makeQuery(id+"F21.imprint","IMPRINT",FACE,{"disambiguationData":[TD([[makeQuery(id+"F21.imprint","IMPRINT",EDGE,{"derivedFrom":sQuery(id+"F21.wireOp",EDGE,"E36.MirrorCS")}),1.0]])]});
            var Q1;
            {var subQ0=sQuery(id+"F21.wireOp",EDGE,"E33.top");Q1=makeQuery(id+"F21.imprint","IMPRINT",FACE,{"disambiguationData":[TD([[makeQuery(id+"F21.imprint","IMPRINT",EDGE,{"derivedFrom":subQ0}),1.0]])]});}
            var Q2;
            Q2=makeQuery(id+"F21.imprint","IMPRINT",FACE,{"disambiguationData":[TD([[makeQuery(id+"F21.imprint","IMPRINT",EDGE,{"derivedFrom":sQuery(id+"F21.wireOp",EDGE,"E33.bottom")}),1.0]])]});
            var Q3;
            {var subQ0=sQuery(id+"F21.wireOp",EDGE,"E33.bottom");Q3=makeQuery(id+"F21.imprint","IMPRINT",FACE,{"disambiguationData":[TD([[makeQuery(id+"F21.imprint","IMPRINT",EDGE,{"derivedFrom":subQ0}),-1.0]])]});}
            extrude(context, id + "F23", {"entities" : qUnion([Q0, Q1, Q2, Q3]), "operationType" : NewBodyOperationType.REMOVE, "oppositeDirection" : true, "depth" : 2.54 * mm});
        }
        {
            var Q0;
            {var subQ0=sQuery(id+"F0.wireOp",EDGE,"E18.right");var subQ1=sQuery(id+"F21.wireOp",EDGE,"E34");Q0=makeQuery(id+"F22.boolean.opBoolean","SPLIT",EDGE,{"disambiguationData":[topologyDisambiguationEdgeConnected([makeQuery(id+"F1.opExtrude","SWEPT_FACE",FACE,{"disambiguationData":[OSD([subQ0])]})])],"derivedFrom":makeQuery(id+"F22.opExtrude","SWEPT_EDGE",EDGE,{"disambiguationData":[OSD([subQ1,sQuery(id+"F21.wireOp",EDGE,"E42")])]})});}
            var Q1;
            Q1=makeQuery(id+"F22.opExtrude","SWEPT_EDGE",EDGE,{"disambiguationData":[OSD([sQuery(id+"F21.wireOp",EDGE,"E33.bottom"),sQuery(id+"F21.wireOp",EDGE,"E33.right"),sQuery(id+"F21.wireOp",EDGE,"E34")])]});
            var Q2;
            Q2=makeQuery(id+"F22.opExtrude","SWEPT_EDGE",EDGE,{"disambiguationData":[OSD([sQuery(id+"F21.wireOp",EDGE,"E33.top"),sQuery(id+"F21.wireOp",EDGE,"E33.right"),sQuery(id+"F21.wireOp",EDGE,"E35")])]});
            var Q3;
            {var subQ0=sQuery(id+"F0.wireOp",EDGE,"E18.right");var subQ1=sQuery(id+"F21.wireOp",EDGE,"E35");Q3=makeQuery(id+"F22.boolean.opBoolean","SPLIT",EDGE,{"disambiguationData":[topologyDisambiguationEdgeConnected([makeQuery(id+"F1.opExtrude","SWEPT_FACE",FACE,{"disambiguationData":[OSD([subQ0])]})])],"derivedFrom":makeQuery(id+"F22.opExtrude","SWEPT_EDGE",EDGE,{"disambiguationData":[OSD([subQ1,sQuery(id+"F21.wireOp",EDGE,"E42")])]})});}
            var Q4;
            {var subQ0=sQuery(id+"F0.wireOp",EDGE,"E18.left");var subQ1=sQuery(id+"F21.wireOp",EDGE,"E36.MirrorCS");Q4=makeQuery(id+"F22.boolean.opBoolean","SPLIT",EDGE,{"disambiguationData":[topologyDisambiguationEdgeConnected([makeQuery(id+"F1.opExtrude","SWEPT_FACE",FACE,{"disambiguationData":[OSD([subQ0])]})])],"derivedFrom":makeQuery(id+"F22.opExtrude","SWEPT_EDGE",EDGE,{"disambiguationData":[OSD([subQ1,sQuery(id+"F21.wireOp",EDGE,"E39")])]})});}
            var Q5;
            Q5=makeQuery(id+"F22.opExtrude","SWEPT_EDGE",EDGE,{"disambiguationData":[OSD([sQuery(id+"F21.wireOp",EDGE,"E36.MirrorCS"),sQuery(id+"F21.wireOp",EDGE,"E37.MirrorCS")])]});
            var Q6;
            Q6=makeQuery(id+"F22.opExtrude","SWEPT_EDGE",EDGE,{"disambiguationData":[OSD([sQuery(id+"F21.wireOp",EDGE,"E37.MirrorCS"),sQuery(id+"F21.wireOp",EDGE,"E38.MirrorCS")])]});
            var Q7;
            {var subQ0=sQuery(id+"F0.wireOp",EDGE,"E18.left");var subQ1=sQuery(id+"F21.wireOp",EDGE,"E38.MirrorCS");Q7=makeQuery(id+"F22.boolean.opBoolean","SPLIT",EDGE,{"disambiguationData":[topologyDisambiguationEdgeConnected([makeQuery(id+"F1.opExtrude","SWEPT_FACE",FACE,{"disambiguationData":[OSD([subQ0])]})])],"derivedFrom":makeQuery(id+"F22.opExtrude","SWEPT_EDGE",EDGE,{"disambiguationData":[OSD([subQ1,sQuery(id+"F21.wireOp",EDGE,"E39")])]})});}
            fillet(context, id + "F24", {"entities" : qUnion([Q0, Q1, Q2, Q3, Q4, Q5, Q6, Q7]), "radius" : 5.08 * mm, "tangentPropagation" : true, "allowEdgeOverflow" : false});
        }
        {
            var Q0;
            Q0=makeQuery(id+"F22.opExtrude","CAP_FACE",FACE,{"disambiguationData":[OSD([sQuery(id+"F21.wireOp",EDGE,"E33.right"),sQuery(id+"F21.wireOp",EDGE,"E34"),sQuery(id+"F21.wireOp",EDGE,"E35"),sQuery(id+"F21.wireOp",EDGE,"E40"),sQuery(id+"F21.wireOp",EDGE,"E42")])],"isStart":false});
            var Q1;
            Q1=makeQuery(id+"F23.boolean.opBoolean","COPY",EDGE,{"derivedFrom":makeQuery(id+"F23.opExtrude","CAP_EDGE",EDGE,{"disambiguationData":[OSD([sQuery(id+"F21.wireOp",EDGE,"E40")])],"isStart":false})});
            var Q2;
            Q2=makeQuery(id+"F23.boolean.opBoolean","COPY",EDGE,{"derivedFrom":makeQuery(id+"F23.opExtrude","CAP_EDGE",EDGE,{"disambiguationData":[OSD([sQuery(id+"F21.wireOp",EDGE,"E41.MirrorC")])],"isStart":false})});
            var Q3;
            Q3=makeQuery(id+"F22.opExtrude","CAP_FACE",FACE,{"disambiguationData":[OSD([sQuery(id+"F21.wireOp",EDGE,"E36.MirrorCS"),sQuery(id+"F21.wireOp",EDGE,"E37.MirrorCS"),sQuery(id+"F21.wireOp",EDGE,"E38.MirrorCS"),sQuery(id+"F21.wireOp",EDGE,"E39"),sQuery(id+"F21.wireOp",EDGE,"E41.MirrorC")])],"isStart":false});
            fillet(context, id + "F25", {"entities" : qUnion([Q0, Q1, Q2, Q3]), "radius" : 0.76 * mm, "tangentPropagation" : true, "allowEdgeOverflow" : false});
        }
        {
            var Q0;
            {var subQ0=sQuery(id+"F0.wireOp",EDGE,"E18.top");Q0=makeQuery(id+"F4.boolean.opBoolean","MERGE",FACE,{"derivedFrom":[makeQuery(id+"F1.opExtrude","CAP_FACE",FACE,{"disambiguationData":[OSD([sQuery(id+"F0.wireOp",EDGE,"E0.left"),sQuery(id+"F0.wireOp",EDGE,"E0.right"),sQuery(id+"F0.wireOp",EDGE,"E1.top"),sQuery(id+"F0.wireOp",EDGE,"E3"),sQuery(id+"F0.wireOp",EDGE,"E4"),sQuery(id+"F0.wireOp",EDGE,"E6.MirrorCS"),sQuery(id+"F0.wireOp",EDGE,"E7.MirrorCS"),sQuery(id+"F0.wireOp",EDGE,"E8.MirrorCS"),sQuery(id+"F0.wireOp",EDGE,"E9.MirrorCS"),sQuery(id+"F0.wireOp",EDGE,"E10.MirrorCS"),sQuery(id+"F0.wireOp",EDGE,"E11.MirrorCS"),sQuery(id+"F0.wireOp",EDGE,"E12.MirrorCS"),sQuery(id+"F0.wireOp",EDGE,"E13.MirrorCS"),sQuery(id+"F0.wireOp",EDGE,"E14.MirrorCS"),sQuery(id+"F0.wireOp",EDGE,"E18.bottom"),subQ0,sQuery(id+"F0.wireOp",EDGE,"E18.left"),sQuery(id+"F0.wireOp",EDGE,"E18.right")])],"isStart":false}),makeQuery(id+"F4.opExtrude","SWEPT_FACE",FACE,{"disambiguationData":[OSD([subQ0]),TDD([makeQuery(id+"F1.opExtrude","CAP_EDGE",EDGE,{"disambiguationData":[OSD([subQ0])],"isStart":false})])]})]});}
            var sketch = newSketch(context, id + "F26", { "sketchPlane" : qUnion([Q0])});
            skLineSegment(sketch, "E43.0", {"start": v(-10.7, -41.1) * mm, "end": v(-14.96, -41.1) * mm});
            skArc(sketch, "E44.0", {"start": v(-15.86, -40.72) * mm, "mid": v(-15.45, -41) * mm, "end": v(-14.96, -41.1) * mm});
            skArc(sketch, "E45.0", {"start": v(-16.23, -39.83) * mm, "mid": v(-16.13, -40.31) * mm, "end": v(-15.86, -40.72) * mm});
            skLineSegment(sketch, "E46.0", {"start": v(-16.23, -44.39) * mm, "end": v(-16.23, 44.39) * mm});
            skLineSegment(sketch, "E47.0", {"start": v(-12.94, -41.1) * mm, "end": v(-12.94, 27.53) * mm});
            skLineSegment(sketch, "E48.0", {"start": v(12.94, -41.1) * mm, "end": v(12.94, 27.53) * mm});
            skLineSegment(sketch, "E49.0", {"start": v(16.23, -44.39) * mm, "end": v(16.23, 44.39) * mm});
            skArc(sketch, "E50.0", {"start": v(15.86, -40.72) * mm, "mid": v(16.13, -40.31) * mm, "end": v(16.23, -39.83) * mm});
            skArc(sketch, "E51.0", {"start": v(14.96, -41.1) * mm, "mid": v(15.45, -41) * mm, "end": v(15.86, -40.72) * mm});
            skLineSegment(sketch, "E52.0", {"start": v(14.96, -41.1) * mm, "end": v(10.7, -41.1) * mm});
            skLineSegment(sketch, "E53.0", {"start": v(-14.96, 52) * mm, "end": v(14.96, 52) * mm});
            skArc(sketch, "E54.0", {"start": v(-16.23, 50.74) * mm, "mid": v(-15.86, 51.63) * mm, "end": v(-14.96, 52) * mm});
            skArc(sketch, "E55.0", {"start": v(14.96, 52) * mm, "mid": v(15.86, 51.63) * mm, "end": v(16.23, 50.74) * mm});
            skLineSegment(sketch, "E56", {"start": v(-16.23, 50.74) * mm, "end": v(-16.23, 44.39) * mm});
            skLineSegment(sketch, "E57", {"start": v(16.23, 50.74) * mm, "end": v(16.23, 44.39) * mm});
            skPoint(sketch, "E58.orphan", {"position": v(-12.94, -27.53) * mm});
            skPoint(sketch, "E59.orphan", {"position": v(12.94, -27.53) * mm});
            skPoint(sketch, "E60.0", {"position": v(-12.94, 41.05) * mm});
            skPoint(sketch, "E61.0", {"position": v(12.94, 41.1) * mm});
            skLineSegment(sketch, "E62", {"start": v(-12.94, 27.53) * mm, "end": v(-12.94, 41.05) * mm});
            skLineSegment(sketch, "E63", {"start": v(-12.94, 41.05) * mm, "end": v(12.94, 41.1) * mm});
            skLineSegment(sketch, "E64", {"start": v(12.94, 41.1) * mm, "end": v(12.94, 27.53) * mm});
            skSolve(sketch);
        }
        {
            var Q0;
            {var subQ0=sQuery(id+"F0.wireOp",EDGE,"E18.top");var subQ1=makeQuery(id+"F1.opExtrude","CAP_EDGE",EDGE,{"disambiguationData":[OSD([subQ0])],"isStart":false});var subQ2=sQuery(id+"F0.wireOp",EDGE,"E18.right");var subQ3=sQuery(id+"F0.wireOp",EDGE,"E18.left");var subQ4=sQuery(id+"F0.wireOp",EDGE,"E14.MirrorCS");var subQ5=sQuery(id+"F0.wireOp",EDGE,"E13.MirrorCS");var subQ6=sQuery(id+"F0.wireOp",EDGE,"E12.MirrorCS");var subQ7=sQuery(id+"F0.wireOp",EDGE,"E11.MirrorCS");var subQ8=sQuery(id+"F0.wireOp",EDGE,"E10.MirrorCS");var subQ9=sQuery(id+"F0.wireOp",EDGE,"E9.MirrorCS");var subQ10=sQuery(id+"F0.wireOp",EDGE,"E8.MirrorCS");var subQ11=sQuery(id+"F0.wireOp",EDGE,"E1.top");var subQ12=sQuery(id+"F0.wireOp",EDGE,"E0.right");var subQ13=sQuery(id+"F0.wireOp",EDGE,"E0.left");var subQ14=makeQuery(id+"F1.opExtrude","CAP_FACE",FACE,{"disambiguationData":[OSD([subQ13,subQ12,subQ11,sQuery(id+"F0.wireOp",EDGE,"E3"),sQuery(id+"F0.wireOp",EDGE,"E4"),sQuery(id+"F0.wireOp",EDGE,"E6.MirrorCS"),sQuery(id+"F0.wireOp",EDGE,"E7.MirrorCS"),subQ10,subQ9,subQ8,subQ7,subQ6,subQ5,subQ4,sQuery(id+"F0.wireOp",EDGE,"E18.bottom"),subQ0,subQ3,subQ2])],"isStart":false});var subQ15=makeQuery(id+"F4.boolean.opBoolean","MERGE",FACE,{"derivedFrom":[subQ14,makeQuery(id+"F4.opExtrude","SWEPT_FACE",FACE,{"disambiguationData":[OSD([subQ0]),TDD([subQ1])]})]});var subQ16=subQ15;var subQ18=makeQuery(id+"F19.opChamfer","BLEND_EDGE",EDGE,{"blendedFrom":[makeQuery(id+"F1.opExtrude","CAP_EDGE",EDGE,{"disambiguationData":[OSD([subQ13])],"isStart":false}),subQ16],"blendedInto":[subQ16]});Q0=makeQuery(id+"F26.imprint","IMPRINT",FACE,{"disambiguationData":[TD([[makeQuery(id+"F26.imprint","IMPRINT",EDGE,{"derivedFrom":subQ18}),1.0]])]});}
            var Q1;
            {var subQ0=sQuery(id+"F0.wireOp",EDGE,"E18.top");var subQ1=sQuery(id+"F0.wireOp",EDGE,"E9.MirrorCS");var subQ2=sQuery(id+"F0.wireOp",EDGE,"E8.MirrorCS");var subQ3=sQuery(id+"F0.wireOp",EDGE,"E0.right");var subQ4=makeQuery(id+"F4.boolean.opBoolean","MERGE",FACE,{"derivedFrom":[makeQuery(id+"F1.opExtrude","CAP_FACE",FACE,{"disambiguationData":[OSD([sQuery(id+"F0.wireOp",EDGE,"E0.left"),subQ3,sQuery(id+"F0.wireOp",EDGE,"E1.top"),sQuery(id+"F0.wireOp",EDGE,"E3"),sQuery(id+"F0.wireOp",EDGE,"E4"),sQuery(id+"F0.wireOp",EDGE,"E6.MirrorCS"),sQuery(id+"F0.wireOp",EDGE,"E7.MirrorCS"),subQ2,subQ1,sQuery(id+"F0.wireOp",EDGE,"E10.MirrorCS"),sQuery(id+"F0.wireOp",EDGE,"E11.MirrorCS"),sQuery(id+"F0.wireOp",EDGE,"E12.MirrorCS"),sQuery(id+"F0.wireOp",EDGE,"E13.MirrorCS"),sQuery(id+"F0.wireOp",EDGE,"E14.MirrorCS"),sQuery(id+"F0.wireOp",EDGE,"E18.bottom"),subQ0,sQuery(id+"F0.wireOp",EDGE,"E18.left"),sQuery(id+"F0.wireOp",EDGE,"E18.right")])],"isStart":false}),makeQuery(id+"F4.opExtrude","SWEPT_FACE",FACE,{"disambiguationData":[OSD([subQ0]),TDD([makeQuery(id+"F1.opExtrude","CAP_EDGE",EDGE,{"disambiguationData":[OSD([subQ0])],"isStart":false})])]})]});var subQ5=subQ4;var subQ7=makeQuery(id+"F19.opChamfer","BLEND_EDGE",EDGE,{"blendedFrom":[makeQuery(id+"F1.opExtrude","CAP_EDGE",EDGE,{"disambiguationData":[OSD([subQ3])],"isStart":false}),subQ5],"blendedInto":[subQ5]});Q1=makeQuery(id+"F26.imprint","IMPRINT",FACE,{"disambiguationData":[TD([[makeQuery(id+"F26.imprint","IMPRINT",EDGE,{"derivedFrom":subQ7}),-1.0]])]});}
            var Q2;
            {var subQ0=sQuery(id+"F0.wireOp",EDGE,"E18.top");var subQ1=sQuery(id+"F0.wireOp",EDGE,"E14.MirrorCS");var subQ2=sQuery(id+"F0.wireOp",EDGE,"E1.top");var subQ3=sQuery(id+"F0.wireOp",EDGE,"E0.left");var subQ4=makeQuery(id+"F4.boolean.opBoolean","MERGE",FACE,{"derivedFrom":[makeQuery(id+"F1.opExtrude","CAP_FACE",FACE,{"disambiguationData":[OSD([subQ3,sQuery(id+"F0.wireOp",EDGE,"E0.right"),subQ2,sQuery(id+"F0.wireOp",EDGE,"E3"),sQuery(id+"F0.wireOp",EDGE,"E4"),sQuery(id+"F0.wireOp",EDGE,"E6.MirrorCS"),sQuery(id+"F0.wireOp",EDGE,"E7.MirrorCS"),sQuery(id+"F0.wireOp",EDGE,"E8.MirrorCS"),sQuery(id+"F0.wireOp",EDGE,"E9.MirrorCS"),sQuery(id+"F0.wireOp",EDGE,"E10.MirrorCS"),sQuery(id+"F0.wireOp",EDGE,"E11.MirrorCS"),sQuery(id+"F0.wireOp",EDGE,"E12.MirrorCS"),sQuery(id+"F0.wireOp",EDGE,"E13.MirrorCS"),subQ1,sQuery(id+"F0.wireOp",EDGE,"E18.bottom"),subQ0,sQuery(id+"F0.wireOp",EDGE,"E18.left"),sQuery(id+"F0.wireOp",EDGE,"E18.right")])],"isStart":false}),makeQuery(id+"F4.opExtrude","SWEPT_FACE",FACE,{"disambiguationData":[OSD([subQ0]),TDD([makeQuery(id+"F1.opExtrude","CAP_EDGE",EDGE,{"disambiguationData":[OSD([subQ0])],"isStart":false})])]})]});var subQ5=subQ4;var subQ7=makeQuery(id+"F19.opChamfer","BLEND_EDGE",EDGE,{"blendedFrom":[makeQuery(id+"F1.opExtrude","CAP_EDGE",EDGE,{"disambiguationData":[OSD([subQ3])],"isStart":false}),subQ5],"blendedInto":[subQ5]});Q2=makeQuery(id+"F26.imprint","IMPRINT",FACE,{"disambiguationData":[TD([[makeQuery(id+"F26.imprint","IMPRINT",EDGE,{"derivedFrom":subQ7}),-1.0]])]});}
            var Q3;
            {var subQ24=sQuery(id+"F26.wireOp",EDGE,"E44.0");Q3=makeQuery(id+"F26.imprint","IMPRINT",FACE,{"disambiguationData":[TD([[makeQuery(id+"F26.imprint","IMPRINT",EDGE,{"derivedFrom":subQ24}),1.0]])]});}
            extrude(context, id + "F27", {"entities" : qUnion([Q0, Q1, Q2, Q3]), "operationType" : NewBodyOperationType.ADD, "depth" : 22.86 * mm, "hasSecondDirection" : true, "secondDirectionOppositeDirection" : true, "secondDirectionDepth" : 2.54 * mm});
        }
    });
